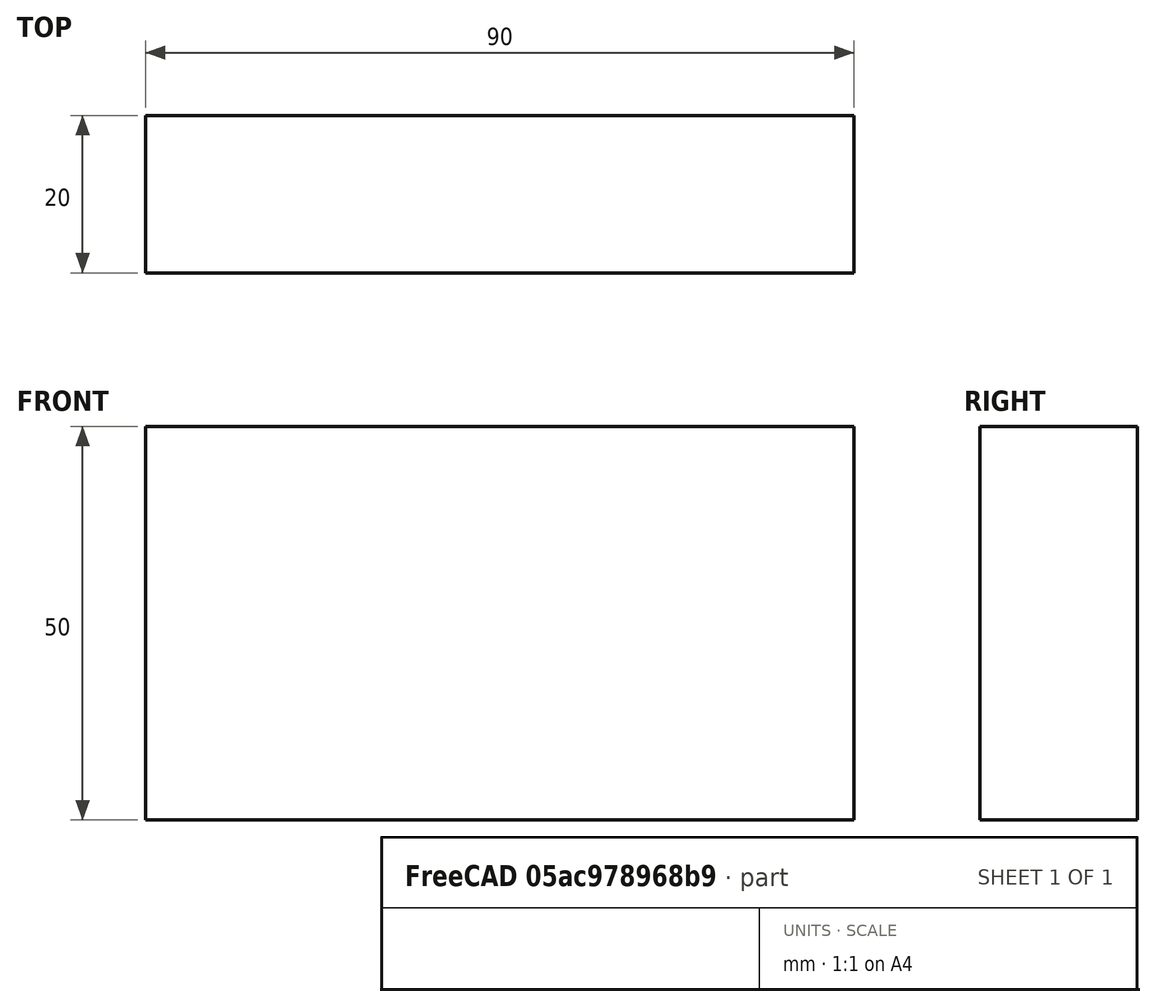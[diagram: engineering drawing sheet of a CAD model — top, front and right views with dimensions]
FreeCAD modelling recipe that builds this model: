
FCSTD DOCUMENT  (FreeCAD 0.15R4671 (Git))
Label: Flat Bar 90x20 EN10058 S235JR
License: All rights reserved
LicenseURL: http://en.wikipedia.org/wiki/All_rights_reserved
objects: Sketcher::SketchObject×1, Part::Extrusion×1
note: 2 computed .brp shape members not serialized (recipe doc carries the construction recipe); baked Part::Feature solids carry a one-line shape summary decoded from their .brp

FEATURE [Sketcher::SketchObject] Sketch
  sketch-geometry (4):
    g0: LineSegment StartX=-45 StartY=-10 StartZ=0 EndX=45 EndY=-10 EndZ=0
    g1: LineSegment StartX=45 StartY=-10 StartZ=0 EndX=45 EndY=10 EndZ=0
    g2: LineSegment StartX=45 StartY=10 StartZ=0 EndX=-45 EndY=10 EndZ=0
    g3: LineSegment StartX=-45 StartY=10 StartZ=0 EndX=-45 EndY=-10 EndZ=0
  constraints (12):
    c: Coincident(g0,g1)
    c: Coincident(g1,g2)
    c: Coincident(g2,g3)
    c: Coincident(g3,g0)
    c: Horizontal(g0)
    c: Horizontal(g2)
    c: Vertical(g1)
    c: Vertical(g3)
    c: Symmetric(g1,g2,g-2)
    c: Symmetric(g0,g1,g-1)
    c: DistanceY(g1) = 20
    c: DistanceX(g0) = 90
FEATURE [Part::Extrusion] Extrude  label="Flat Bar 90x20 EN10058 S235JR"
  Base = -> Sketch
  Dir = (0,0,50)
  Solid = true
